# Revit family: NBS_Allermuir_OffcChrs_AxylChair
name_source: partatom
category: Furniture
revit_build: Autodesk Revit 2016 (Build: 20151007_0715(x64)
units: mm (PartAtom-declared; Revit-internal decimal feet)

## family parameters
Always vertical = Yes
Cut with Voids When Loaded = No
Room Calculation Point = No
Shared = No
Work Plane-Based = No

## types (1)
- AXL02
    AssetType = Moveable
    BIMObjectName = NBS_Allermuir_OfficeChairs_Axyl_AXL02
    Category = Pr_40_50_12_57:Office chairs
    Description = Arm chair
    DurationUnit = year
    ExpectedLife = 5
    Features = Stacks 4, Stacking buffers, Plastic Glides
    FootHeight = 5 mm  [stored 0.0164042 ft]
    FrameColour = Black, white, sage, basalt, peacock blue, coral, pebble, stone, polished aluminium, raw aluminium
    FrameFinishOptions = Powder coat, polished aluminium, raw aluminium
    FrameMaterials = Aluminium
    FrameMountingMaterial = NBS_Concept
    HighestSeatingHeight = 0 mm  [stored 0 ft]
    IfcExportAs = IfcFurnitureType
    IfcExportType = CHAIR
    IsBuiltIn = No
    LegHeight = 377 mm  [stored 1.23688 ft]
    LowestSeatingHeight = 0 mm  [stored 0 ft]
    ManufacturerName = Allermuir
    ManufacturerURL = www.senator.co.uk
    Material = Aluminium
    ModelNumber = AXL02
    ModelReference = Axyl
    NBSCertification = www.nationalbimlibrary.com/cert/v4lcurhw
    NBSDescription = Office chairs
    NBSReference = 45-35-20/330
    Name = OfficeChairs_Axyl_AXL02_Allermuir
    NominalDepth = 605 mm
    NominalHeight = 780 mm
    NominalLength = 565 mm
    NominalWidth = 605 mm
    OptionalFeatures = Glides with felt
    SeatFrameMaterial = NBS_Concept
    SeatingHeight = 450 mm  [stored 1.47638 ft]
    SeatingSeatMaterial = NBS_Concept
    SeatsAndBacksColour = Black, white, sage, basalt, peacock blue, coral (plastic); pebble, stone (wood fibre)
    SeatsAndBacksMaterial = Plastic
    SeatsAndBacksMaterialOptions = Plastic, Wood fibre injected plastic
    Size = 565 x 605 x 780 mm
    StandardsDurability = BS EN 16139
    StandardsSafetyRequirements = BS EN 16139
    Status = UNSET
    Uniclass2015Code = Pr_40_50_12_57
    Uniclass2015Title = Office chairs
    Uniclass2015Version = Products v1.9
    Version = 1
    WarrantyDescription = Allermuir warrant that its manufactured products are free from manufacturing defects - in materials or workmanship - for a period of five (5) years. , Allermuir will repair, or replace (at Allermuir's sole discretion) with comparable free of charge materials / components, any product / component which fails under normal use in a single shift environment, as a result of a defect in the materials and/ or workmanship
    WarrantyDurationParts = 5
    WarrantyDurationUnit = year

note: [stored X ft] marks values corroborated as IEEE doubles in the binary element streams (Revit-internal decimal feet)

## geometry (parser evidence)
native form markers: Sweep x10
no freeform markers — native parametric forms only
